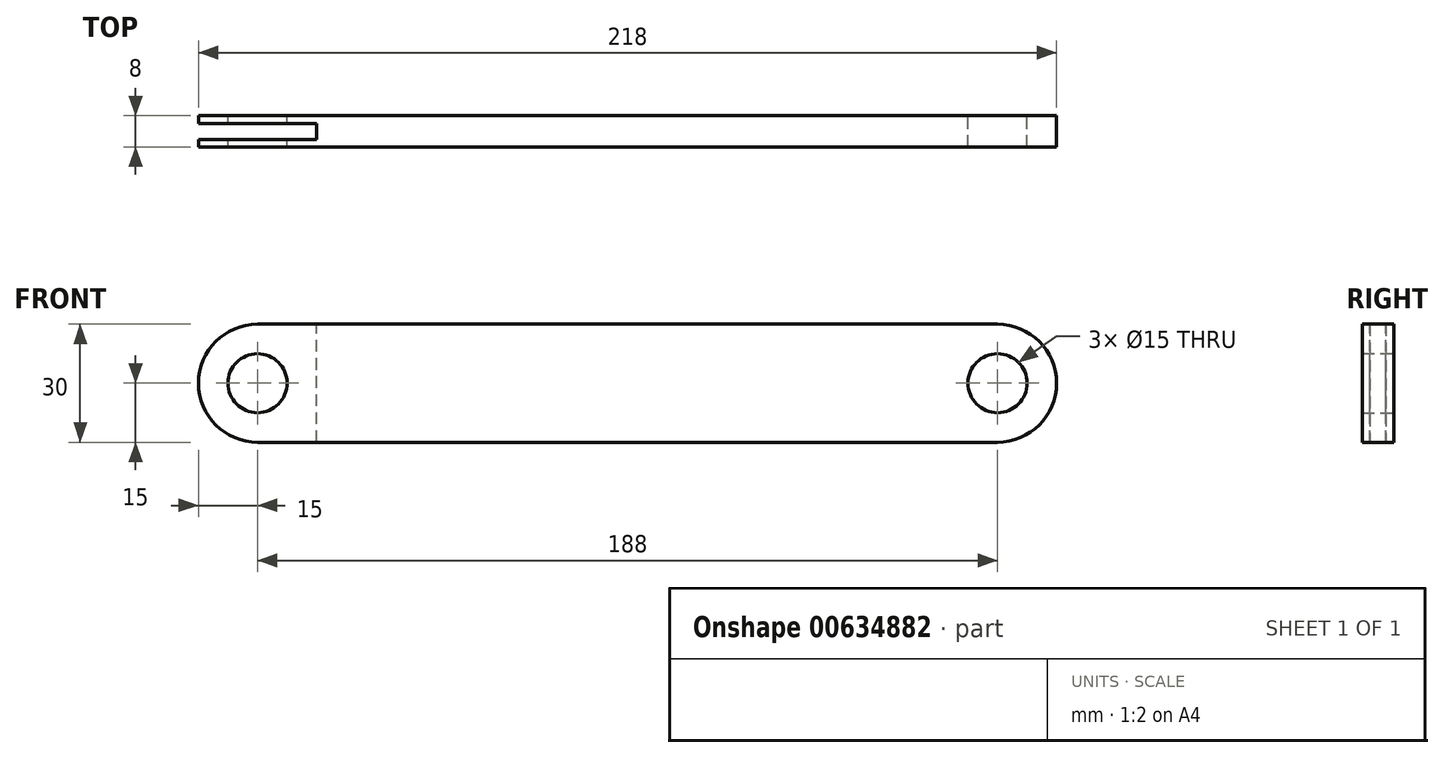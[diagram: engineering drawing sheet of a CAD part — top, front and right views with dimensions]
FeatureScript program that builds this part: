
annotation { "Feature Type Name" : "Feature", "Feature Type Description" : "" }
export const myFeature = defineFeature(function(context is Context, id is Id, definition is map)
    precondition{}
    {
        {
            var Q0;
            Q0=qCreatedBy(makeId("Front.planeOp"),FACE);
            var sketch = newSketch(context, id + "F0", { "sketchPlane" : qUnion([Q0])});
            skArc(sketch, "E0", {"start": v(0, 15) * mm, "mid": v(-15, 0) * mm, "end": v(0, -15) * mm});
            skArc(sketch, "E1", {"start": v(188, -15) * mm, "mid": v(203, 0) * mm, "end": v(188, 15) * mm});
            skLineSegment(sketch, "E2", {"start": v(0, 15) * mm, "end": v(188, 15) * mm});
            skLineSegment(sketch, "E3", {"start": v(0, -15) * mm, "end": v(188, -15) * mm});
            skSolve(sketch);
        }
        {
            var Q0;
            Q0=makeQuery(id+"F0.imprint","IMPRINT",FACE,{"disambiguationData":[TD([[makeQuery(id+"F0.imprint","IMPRINT",EDGE,{"derivedFrom":sQuery(id+"F0.wireOp",EDGE,"E0")}),1.0]])]});
            extrude(context, id + "F1", {"entities" : qUnion([Q0]), "depth" : 8 * mm, "offsetDistance" : 25 * mm});
        }
        {
            var Q0;
            Q0=sQuery(id+"F0.wireOp",VERTEX,"E0.center");
            var Q1;
            Q1=makeQuery(id+"F1.opExtrude","SWEPT_BODY",BODY,{"disambiguationData":[OSD([sQuery(id+"F0.wireOp",EDGE,"E0"),sQuery(id+"F0.wireOp",EDGE,"E1"),sQuery(id+"F0.wireOp",EDGE,"E2"),sQuery(id+"F0.wireOp",EDGE,"E3")])]});
            hole(context, id + "F2", {"style" : HoleStyle.SIMPLE, "endStyle" : HoleEndStyle.THROUGH, "oppositeDirection" : true, "standardTappedOrClearance" : lookupTablePath({ "fit" : "Normal", "standard" : "Custom", "size" : "M5", "type" : "Clearance" }), "standardBlindInLast" : lookupTablePath({ "fit" : "Standard", "standard" : "Custom", "size" : "M5", "type" : "Clearance" }), "holeDiameter" : 15 * mm, "majorDiameter" : 5 * mm, "isTappedThrough" : true, "tappedDepth" : 12 * mm, "tapClearance" : 3, "locations" : qUnion([Q0]), "scope" : qUnion([Q1])});
        }
        {
            var Q0;
            Q0=sQuery(id+"F0.wireOp",VERTEX,"E1.center");
            var Q1;
            Q1=makeQuery(id+"F1.opExtrude","SWEPT_BODY",BODY,{"disambiguationData":[OSD([sQuery(id+"F0.wireOp",EDGE,"E0"),sQuery(id+"F0.wireOp",EDGE,"E1"),sQuery(id+"F0.wireOp",EDGE,"E2"),sQuery(id+"F0.wireOp",EDGE,"E3")])]});
            hole(context, id + "F3", {"style" : HoleStyle.SIMPLE, "endStyle" : HoleEndStyle.THROUGH, "oppositeDirection" : true, "holeDiameter" : 15 * mm, "majorDiameter" : 5 * mm, "isTappedThrough" : true, "tappedDepth" : 12 * mm, "tapClearance" : 3, "locations" : qUnion([Q0]), "scope" : qUnion([Q1])});
        }
        {
            var Q0;
            Q0=qCreatedBy(makeId("Top.planeOp"),FACE);
            cPlane(context, id + "F4", {"entities" : qUnion([Q0]), "cplaneType" : CPlaneType.OFFSET, "offset" : 15 * mm, "width" : 150 * mm, "height" : 150 * mm});
        }
        {
            var Q0;
            Q0=qCreatedBy(id+"F4.planeOp",FACE);
            var sketch = newSketch(context, id + "F5", { "sketchPlane" : qUnion([Q0])});
            skLineSegment(sketch, "E4.bottom", {"start": v(-15, -2.06) * mm, "end": v(15, -2.06) * mm});
            skLineSegment(sketch, "E4.top", {"start": v(-15, -6.06) * mm, "end": v(15, -6.06) * mm});
            skLineSegment(sketch, "E4.left", {"start": v(-15, -2.06) * mm, "end": v(-15, -6.06) * mm});
            skLineSegment(sketch, "E4.right", {"start": v(15, -2.06) * mm, "end": v(15, -6.06) * mm});
            skSolve(sketch);
        }
        {
            var Q0;
            Q0 = qSketchRegion(id + "F5", true);
            var Q1;
            Q1 = qBodyType(qCreatedBy(id + "F5" ,EDGE), BodyType.WIRE);
            extrude(context, id + "F6", {"entities" : qUnion([Q0]), "operationType" : NewBodyOperationType.REMOVE, "surfaceEntities" : qUnion([Q1]), "endBound" : BoundingType.THROUGH_ALL, "oppositeDirection" : true, "depth" : 30 * mm, "offsetDistance" : 25 * mm});
        }
    });
